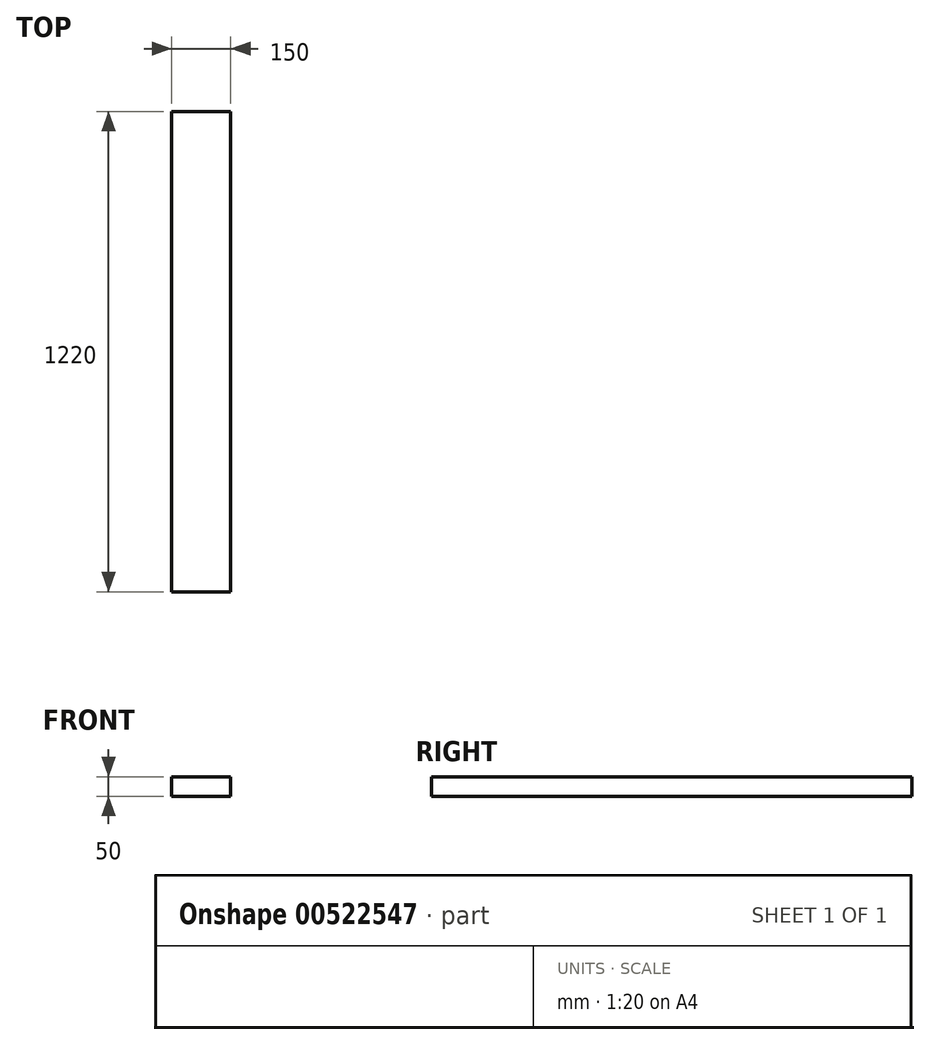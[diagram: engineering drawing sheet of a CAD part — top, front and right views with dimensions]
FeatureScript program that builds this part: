
annotation { "Feature Type Name" : "Feature", "Feature Type Description" : "" }
export const myFeature = defineFeature(function(context is Context, id is Id, definition is map)
    precondition{}
    {
        {
            var Q0;
            Q0=qCreatedBy(makeId("Front.planeOp"),FACE);
            var sketch = newSketch(context, id + "F0", { "sketchPlane" : qUnion([Q0])});
            skLineSegment(sketch, "E0.bottom", {"start": v(-139.39, 44.33) * mm, "end": v(10.61, 44.33) * mm});
            skLineSegment(sketch, "E0.top", {"start": v(-139.39, -5.67) * mm, "end": v(10.61, -5.67) * mm});
            skLineSegment(sketch, "E0.left", {"start": v(-139.39, 44.33) * mm, "end": v(-139.39, -5.67) * mm});
            skLineSegment(sketch, "E0.right", {"start": v(10.61, 44.33) * mm, "end": v(10.61, -5.67) * mm});
            skSolve(sketch);
        }
        {
            var Q0;
            Q0=qSketchRegion(id+"F0",true);
            extrude(context, id + "F1", {"entities" : qUnion([Q0]), "depth" : 1220 * mm, "offsetDistance" : 25 * mm});
        }
    });
